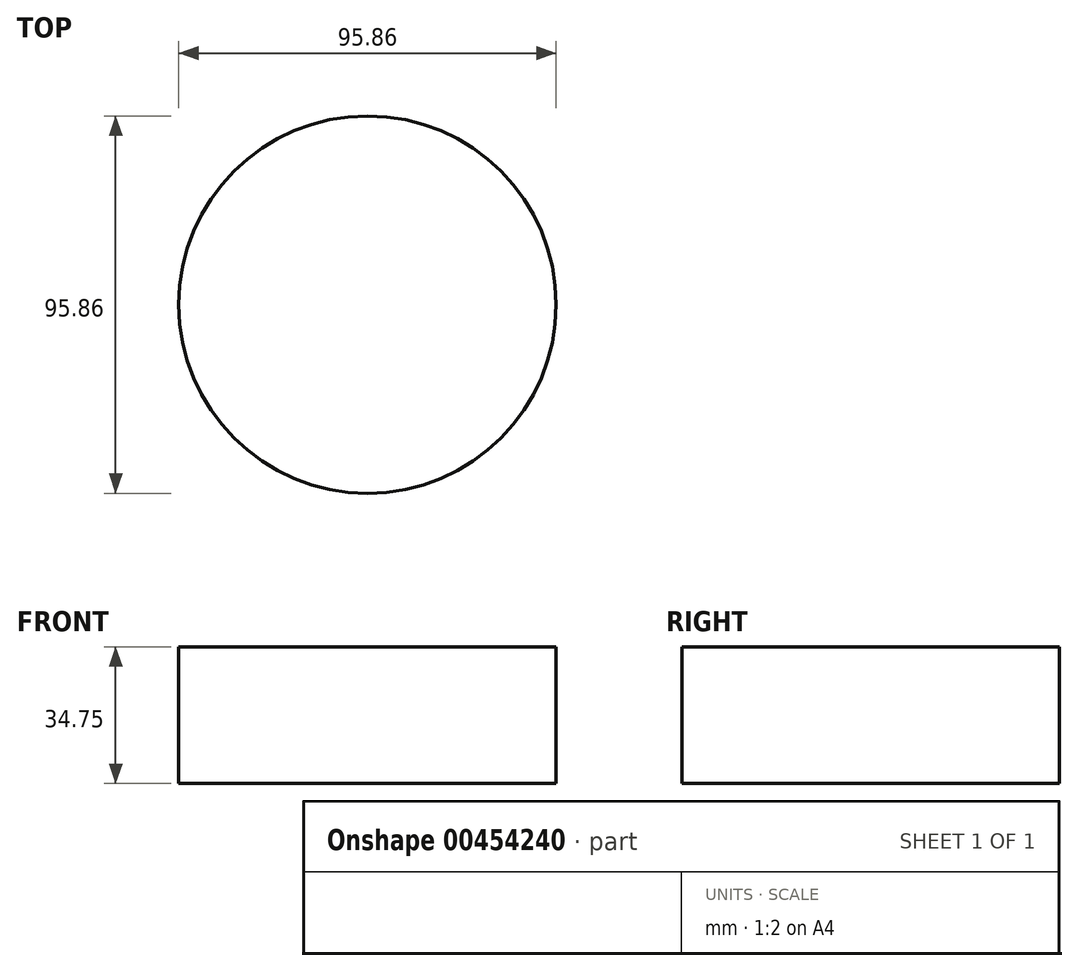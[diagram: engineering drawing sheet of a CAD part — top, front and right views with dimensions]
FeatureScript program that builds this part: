
annotation { "Feature Type Name" : "Feature", "Feature Type Description" : "" }
export const myFeature = defineFeature(function(context is Context, id is Id, definition is map)
    precondition{}
    {
        {
            var Q0;
            Q0=qCreatedBy(makeId("Front.planeOp"),FACE);
            var sketch = newSketch(context, id + "F0", { "sketchPlane" : qUnion([Q0])});
            skLineSegment(sketch, "E0.bottom", {"start": v(0, 0) * mm, "end": v(-47.93, 0) * mm});
            skLineSegment(sketch, "E0.top", {"start": v(0, 34.75) * mm, "end": v(-47.93, 34.75) * mm});
            skLineSegment(sketch, "E0.left", {"start": v(0, 0) * mm, "end": v(0, 34.75) * mm});
            skLineSegment(sketch, "E0.right", {"start": v(-47.93, 0) * mm, "end": v(-47.93, 34.75) * mm});
            skSolve(sketch);
        }
        {
            var Q0;
            Q0=makeQuery(id+"F0.imprint","IMPRINT",FACE,{"disambiguationData":[TD([[makeQuery(id+"F0.imprint","IMPRINT",EDGE,{"derivedFrom":sQuery(id+"F0.wireOp",EDGE,"E0.bottom")}),-1.0]])]});
            var Q1;
            Q1=sQuery(id+"F0.wireOp",EDGE,"E0.left");
            revolve(context, id + "F1", {"entities" : qUnion([Q0]), "axis" : qUnion([Q1]), "revolveType" : RevolveType.FULL});
        }
        {
            var Q0;
            Q0=makeQuery(id+"F1.opRevolve","SWEPT_FACE",FACE,{"disambiguationData":[OSD([sQuery(id+"F0.wireOp",EDGE,"E0.top")])]});
            var sketch = newSketch(context, id + "F2", { "sketchPlane" : qUnion([Q0])});
            skCircle(sketch, "E1", {"center": v(0, 0) * mm, "radius": 20.26 * mm});
            skSolve(sketch);
        }
        {
            var Q0;
            Q0=sQuery(id+"F2.wireOp",EDGE,"E1");
            extrude(context, id + "F3", {"bodyType" : ToolBodyType.SURFACE, "surfaceEntities" : qUnion([Q0]), "depth" : 25 * mm});
        }
    });
